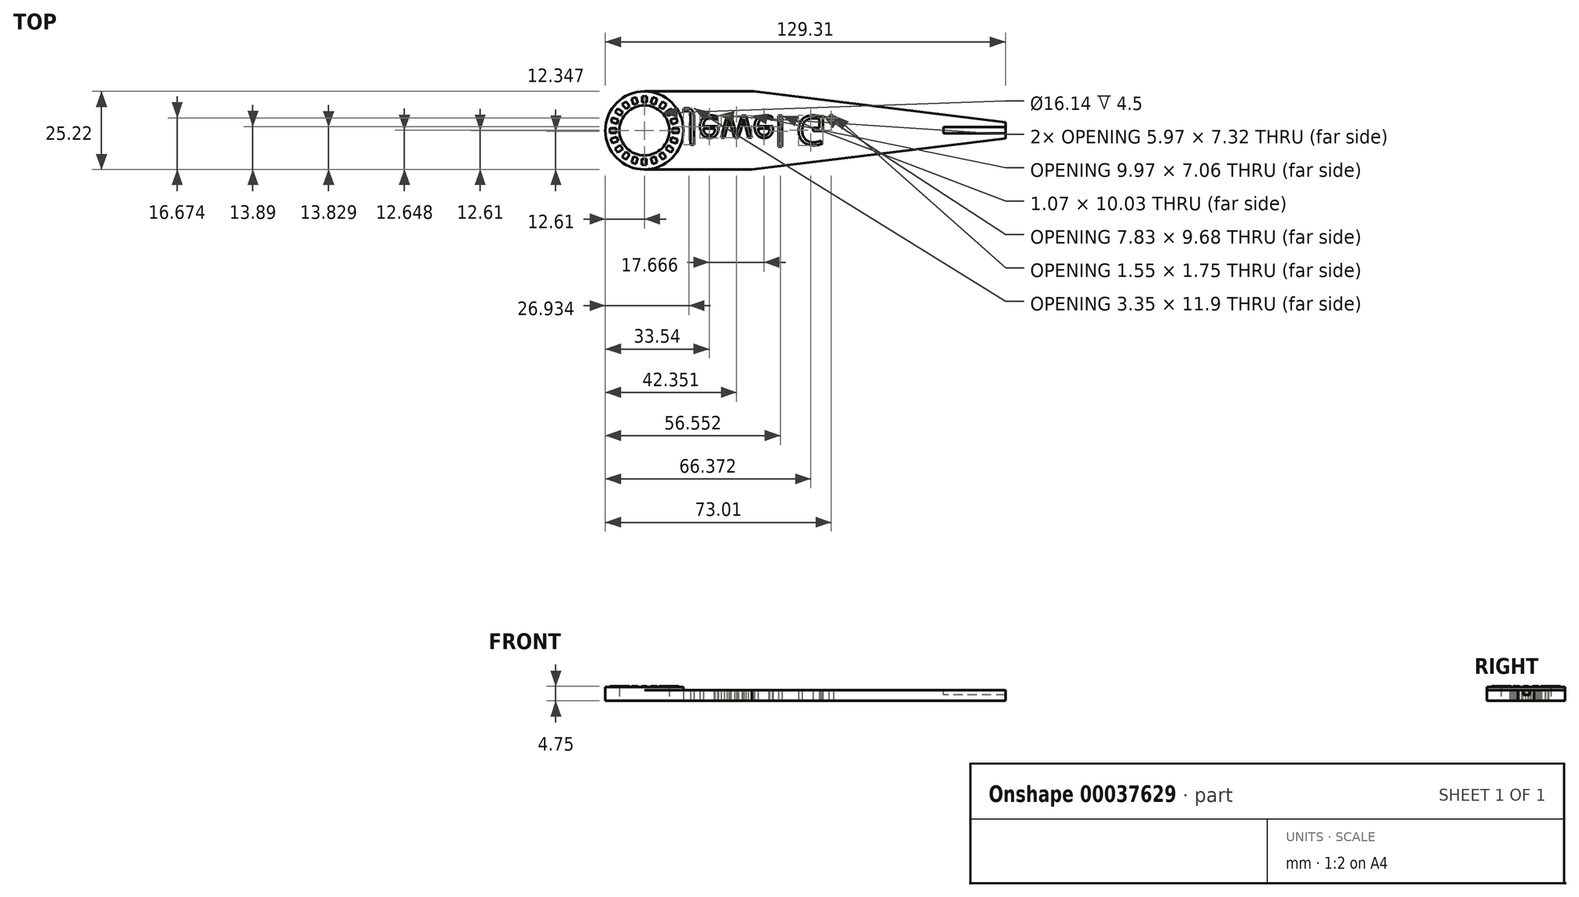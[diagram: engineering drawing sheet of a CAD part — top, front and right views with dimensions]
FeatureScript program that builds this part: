
annotation { "Feature Type Name" : "Feature", "Feature Type Description" : "" }
export const myFeature = defineFeature(function(context is Context, id is Id, definition is map)
    precondition{}
    {
        {
            var Q0;
            Q0=qCreatedBy(makeId("Top.planeOp"),FACE);
            var sketch = newSketch(context, id + "F0", { "sketchPlane" : qUnion([Q0])});
            skCircle(sketch, "E0", {"center": v(0, 0) * mm, "radius": 8.07 * mm});
            skArc(sketch, "E1", {"start": v(0, 12.6) * mm, "mid": v(-12.6, 0) * mm, "end": v(0, -12.6) * mm});
            skLineSegment(sketch, "E2", {"start": v(35.3, 12.6) * mm, "end": v(0, 12.6) * mm});
            skLineSegment(sketch, "E3", {"start": v(34.7, -12.6) * mm, "end": v(0, -12.6) * mm});
            skLineSegment(sketch, "E4", {"start": v(35.3, 12.6) * mm, "end": v(125.73, 12.6) * mm, "construction": true});
            skLineSegment(sketch, "E5", {"start": v(35.3, 12.6) * mm, "end": v(116.7, 2.62) * mm});
            skLineSegment(sketch, "E6.MirrorCS", {"start": v(34.7, -12.6) * mm, "end": v(116.7, -2.62) * mm});
            skLineSegment(sketch, "E7", {"start": v(116.7, 2.62) * mm, "end": v(116.7, -2.62) * mm});
            skSolve(sketch);
        }
        {
            var Q0;
            Q0 = qSketchRegion(id + "F0", true);
            extrude(context, id + "F1", {"entities" : qUnion([Q0]), "depth" : 3.5 * mm});
        }
        {
            var Q0;
            Q0=makeQuery(id+"F1.opExtrude","CAP_FACE",FACE,{"disambiguationData":[OSD([sQuery(id+"F0.wireOp",EDGE,"E0"),sQuery(id+"F0.wireOp",EDGE,"E1"),sQuery(id+"F0.wireOp",EDGE,"E2"),sQuery(id+"F0.wireOp",EDGE,"E3"),sQuery(id+"F0.wireOp",EDGE,"E5"),sQuery(id+"F0.wireOp",EDGE,"E6.MirrorCS"),sQuery(id+"F0.wireOp",EDGE,"E7")])],"isStart":false});
            var sketch = newSketch(context, id + "F2", { "sketchPlane" : qUnion([Q0])});
            skCircle(sketch, "E8", {"center": v(0, 0) * mm, "radius": 8.07 * mm});
            skCircle(sketch, "E9", {"center": v(0, 0) * mm, "radius": 12.6 * mm});
            skSolve(sketch);
        }
        {
            var Q0;
            Q0 = qSketchRegion(id + "F2", true);
            extrude(context, id + "F3", {"entities" : qUnion([Q0]), "operationType" : NewBodyOperationType.ADD, "depth" : 1 * mm});
        }
        {
            var Q0;
            Q0=makeQuery(id+"F3.opExtrude","CAP_FACE",FACE,{"disambiguationData":[OSD([sQuery(id+"F2.wireOp",EDGE,"E8"),sQuery(id+"F2.wireOp",EDGE,"E9")])],"isStart":false});
            var sketch = newSketch(context, id + "F4", { "sketchPlane" : qUnion([Q0])});
            skLineSegment(sketch, "E10.bottom", {"start": v(-0.75, 11.07) * mm, "end": v(0.75, 11.07) * mm});
            skLineSegment(sketch, "E10.top", {"start": v(-0.75, 9.07) * mm, "end": v(0.75, 9.07) * mm});
            skLineSegment(sketch, "E10.left", {"start": v(-0.75, 11.07) * mm, "end": v(-0.75, 9.07) * mm});
            skLineSegment(sketch, "E10.right", {"start": v(0.75, 11.07) * mm, "end": v(0.75, 9.07) * mm});
            skPoint(sketch, "E11", {"position": v(0, 8.07) * mm});
            skLineSegment(sketch, "E12.1.0", {"start": v(-4.14, 10.3) * mm, "end": v(-2.72, 10.77) * mm});
            skLineSegment(sketch, "E12.1.1", {"start": v(-4.14, 10.3) * mm, "end": v(-3.53, 8.4) * mm});
            skLineSegment(sketch, "E12.1.2", {"start": v(-3.53, 8.4) * mm, "end": v(-2.1, 8.87) * mm});
            skLineSegment(sketch, "E12.1.3", {"start": v(-2.72, 10.77) * mm, "end": v(-2.1, 8.87) * mm});
            skLineSegment(sketch, "E12.2.0", {"start": v(-7.14, 8.53) * mm, "end": v(-5.92, 9.4) * mm});
            skLineSegment(sketch, "E12.2.1", {"start": v(-7.14, 8.53) * mm, "end": v(-5.96, 6.9) * mm});
            skLineSegment(sketch, "E12.2.2", {"start": v(-5.96, 6.9) * mm, "end": v(-4.75, 7.8) * mm});
            skLineSegment(sketch, "E12.2.3", {"start": v(-5.92, 9.4) * mm, "end": v(-4.75, 7.8) * mm});
            skLineSegment(sketch, "E12.3.0", {"start": v(-9.43, 5.91) * mm, "end": v(-8.55, 7.13) * mm});
            skLineSegment(sketch, "E12.3.1", {"start": v(-9.43, 5.91) * mm, "end": v(-7.82, 4.74) * mm});
            skLineSegment(sketch, "E12.3.2", {"start": v(-7.82, 4.74) * mm, "end": v(-6.93, 5.95) * mm});
            skLineSegment(sketch, "E12.3.3", {"start": v(-8.55, 7.13) * mm, "end": v(-6.93, 5.95) * mm});
            skLineSegment(sketch, "E12.4.0", {"start": v(-10.8, 2.72) * mm, "end": v(-10.35, 4.14) * mm});
            skLineSegment(sketch, "E12.4.1", {"start": v(-10.8, 2.72) * mm, "end": v(-8.9, 2.1) * mm});
            skLineSegment(sketch, "E12.4.2", {"start": v(-8.9, 2.1) * mm, "end": v(-8.44, 3.52) * mm});
            skLineSegment(sketch, "E12.4.3", {"start": v(-10.35, 4.14) * mm, "end": v(-8.44, 3.52) * mm});
            skLineSegment(sketch, "E12.5.0", {"start": v(-11.13, -0.75) * mm, "end": v(-11.13, 0.75) * mm});
            skLineSegment(sketch, "E12.5.1", {"start": v(-11.13, -0.75) * mm, "end": v(-9.13, -0.75) * mm});
            skLineSegment(sketch, "E12.5.2", {"start": v(-9.13, -0.75) * mm, "end": v(-9.13, 0.75) * mm});
            skLineSegment(sketch, "E12.5.3", {"start": v(-11.13, 0.75) * mm, "end": v(-9.13, 0.75) * mm});
            skLineSegment(sketch, "E12.6.0", {"start": v(-10.36, -4.14) * mm, "end": v(-10.83, -2.72) * mm});
            skLineSegment(sketch, "E12.6.1", {"start": v(-10.36, -4.14) * mm, "end": v(-8.46, -3.53) * mm});
            skLineSegment(sketch, "E12.6.2", {"start": v(-8.46, -3.53) * mm, "end": v(-8.93, -2.1) * mm});
            skLineSegment(sketch, "E12.6.3", {"start": v(-10.83, -2.72) * mm, "end": v(-8.93, -2.1) * mm});
            skLineSegment(sketch, "E12.7.0", {"start": v(-8.59, -7.14) * mm, "end": v(-9.47, -5.92) * mm});
            skLineSegment(sketch, "E12.7.1", {"start": v(-8.59, -7.14) * mm, "end": v(-6.97, -5.96) * mm});
            skLineSegment(sketch, "E12.7.2", {"start": v(-6.97, -5.96) * mm, "end": v(-7.85, -4.75) * mm});
            skLineSegment(sketch, "E12.7.3", {"start": v(-9.47, -5.92) * mm, "end": v(-7.85, -4.75) * mm});
            skLineSegment(sketch, "E12.8.0", {"start": v(-5.97, -9.43) * mm, "end": v(-7.19, -8.55) * mm});
            skLineSegment(sketch, "E12.8.1", {"start": v(-5.97, -9.43) * mm, "end": v(-4.8, -7.82) * mm});
            skLineSegment(sketch, "E12.8.2", {"start": v(-4.8, -7.82) * mm, "end": v(-6.01, -6.93) * mm});
            skLineSegment(sketch, "E12.8.3", {"start": v(-7.19, -8.55) * mm, "end": v(-6.01, -6.93) * mm});
            skLineSegment(sketch, "E12.9.0", {"start": v(-2.78, -10.8) * mm, "end": v(-4.2, -10.35) * mm});
            skLineSegment(sketch, "E12.9.1", {"start": v(-2.78, -10.8) * mm, "end": v(-2.16, -8.9) * mm});
            skLineSegment(sketch, "E12.9.2", {"start": v(-2.16, -8.9) * mm, "end": v(-3.58, -8.44) * mm});
            skLineSegment(sketch, "E12.9.3", {"start": v(-4.2, -10.35) * mm, "end": v(-3.58, -8.44) * mm});
            skLineSegment(sketch, "E12.10.0", {"start": v(0.69, -11.13) * mm, "end": v(-0.81, -11.13) * mm});
            skLineSegment(sketch, "E12.10.1", {"start": v(0.69, -11.13) * mm, "end": v(0.69, -9.13) * mm});
            skLineSegment(sketch, "E12.10.2", {"start": v(0.69, -9.13) * mm, "end": v(-0.81, -9.13) * mm});
            skLineSegment(sketch, "E12.10.3", {"start": v(-0.81, -11.13) * mm, "end": v(-0.81, -9.13) * mm});
            skLineSegment(sketch, "E12.11.0", {"start": v(4.08, -10.36) * mm, "end": v(2.66, -10.83) * mm});
            skLineSegment(sketch, "E12.11.1", {"start": v(4.08, -10.36) * mm, "end": v(3.47, -8.46) * mm});
            skLineSegment(sketch, "E12.11.2", {"start": v(3.47, -8.46) * mm, "end": v(2.04, -8.93) * mm});
            skLineSegment(sketch, "E12.11.3", {"start": v(2.66, -10.83) * mm, "end": v(2.04, -8.93) * mm});
            skLineSegment(sketch, "E12.12.0", {"start": v(7.08, -8.59) * mm, "end": v(5.86, -9.47) * mm});
            skLineSegment(sketch, "E12.12.1", {"start": v(7.08, -8.59) * mm, "end": v(5.9, -6.97) * mm});
            skLineSegment(sketch, "E12.12.2", {"start": v(5.9, -6.97) * mm, "end": v(4.69, -7.85) * mm});
            skLineSegment(sketch, "E12.12.3", {"start": v(5.86, -9.47) * mm, "end": v(4.69, -7.85) * mm});
            skLineSegment(sketch, "E12.13.0", {"start": v(9.37, -5.97) * mm, "end": v(8.5, -7.19) * mm});
            skLineSegment(sketch, "E12.13.1", {"start": v(9.37, -5.97) * mm, "end": v(7.76, -4.8) * mm});
            skLineSegment(sketch, "E12.13.2", {"start": v(7.76, -4.8) * mm, "end": v(6.87, -6.01) * mm});
            skLineSegment(sketch, "E12.13.3", {"start": v(8.5, -7.19) * mm, "end": v(6.87, -6.01) * mm});
            skLineSegment(sketch, "E12.14.0", {"start": v(10.75, -2.78) * mm, "end": v(10.29, -4.2) * mm});
            skLineSegment(sketch, "E12.14.1", {"start": v(10.75, -2.78) * mm, "end": v(8.85, -2.16) * mm});
            skLineSegment(sketch, "E12.14.2", {"start": v(8.85, -2.16) * mm, "end": v(8.38, -3.58) * mm});
            skLineSegment(sketch, "E12.14.3", {"start": v(10.29, -4.2) * mm, "end": v(8.38, -3.58) * mm});
            skLineSegment(sketch, "E12.15.0", {"start": v(11.07, 0.69) * mm, "end": v(11.07, -0.81) * mm});
            skLineSegment(sketch, "E12.15.1", {"start": v(11.07, 0.69) * mm, "end": v(9.07, 0.69) * mm});
            skLineSegment(sketch, "E12.15.2", {"start": v(9.07, 0.69) * mm, "end": v(9.07, -0.81) * mm});
            skLineSegment(sketch, "E12.15.3", {"start": v(11.07, -0.81) * mm, "end": v(9.07, -0.81) * mm});
            skLineSegment(sketch, "E12.16.0", {"start": v(10.3, 4.08) * mm, "end": v(10.77, 2.66) * mm});
            skLineSegment(sketch, "E12.16.1", {"start": v(10.3, 4.08) * mm, "end": v(8.4, 3.47) * mm});
            skLineSegment(sketch, "E12.16.2", {"start": v(8.4, 3.47) * mm, "end": v(8.87, 2.04) * mm});
            skLineSegment(sketch, "E12.16.3", {"start": v(10.77, 2.66) * mm, "end": v(8.87, 2.04) * mm});
            skLineSegment(sketch, "E12.17.0", {"start": v(8.53, 7.08) * mm, "end": v(9.4, 5.86) * mm});
            skLineSegment(sketch, "E12.17.1", {"start": v(8.53, 7.08) * mm, "end": v(6.9, 5.9) * mm});
            skLineSegment(sketch, "E12.17.2", {"start": v(6.9, 5.9) * mm, "end": v(7.8, 4.69) * mm});
            skLineSegment(sketch, "E12.17.3", {"start": v(9.4, 5.86) * mm, "end": v(7.8, 4.69) * mm});
            skLineSegment(sketch, "E12.18.0", {"start": v(5.91, 9.37) * mm, "end": v(7.13, 8.5) * mm});
            skLineSegment(sketch, "E12.18.1", {"start": v(5.91, 9.37) * mm, "end": v(4.74, 7.76) * mm});
            skLineSegment(sketch, "E12.18.2", {"start": v(4.74, 7.76) * mm, "end": v(5.95, 6.87) * mm});
            skLineSegment(sketch, "E12.18.3", {"start": v(7.13, 8.5) * mm, "end": v(5.95, 6.87) * mm});
            skLineSegment(sketch, "E12.19.0", {"start": v(2.72, 10.75) * mm, "end": v(4.14, 10.29) * mm});
            skLineSegment(sketch, "E12.19.1", {"start": v(2.72, 10.75) * mm, "end": v(2.1, 8.85) * mm});
            skLineSegment(sketch, "E12.19.2", {"start": v(2.1, 8.85) * mm, "end": v(3.52, 8.38) * mm});
            skLineSegment(sketch, "E12.19.3", {"start": v(4.14, 10.29) * mm, "end": v(3.52, 8.38) * mm});
            skPoint(sketch, "E12.center", {"position": v(-0.03, -0.03) * mm});
            skSolve(sketch);
        }
        {
            var Q0;
            Q0 = qSketchRegion(id + "F4", true);
            extrude(context, id + "F5", {"entities" : qUnion([Q0]), "operationType" : NewBodyOperationType.ADD, "depth" : .25 * mm});
        }
        {
            var Q0;
            Q0=makeQuery(id+"F1.opExtrude","CAP_FACE",FACE,{"disambiguationData":[OSD([sQuery(id+"F0.wireOp",EDGE,"E0"),sQuery(id+"F0.wireOp",EDGE,"E1"),sQuery(id+"F0.wireOp",EDGE,"E2"),sQuery(id+"F0.wireOp",EDGE,"E3"),sQuery(id+"F0.wireOp",EDGE,"E5"),sQuery(id+"F0.wireOp",EDGE,"E6.MirrorCS"),sQuery(id+"F0.wireOp",EDGE,"E7")])],"isStart":false});
            var sketch = newSketch(context, id + "F6", { "sketchPlane" : qUnion([Q0])});
            skLineSegment(sketch, "E13.bottom", {"start": v(116.7, 1.12) * mm, "end": v(96.7, 1.12) * mm});
            skLineSegment(sketch, "E13.top", {"start": v(116.7, -0.88) * mm, "end": v(96.7, -0.88) * mm});
            skLineSegment(sketch, "E13.left", {"start": v(116.7, 1.12) * mm, "end": v(116.7, -0.88) * mm});
            skLineSegment(sketch, "E13.right", {"start": v(96.7, 1.12) * mm, "end": v(96.7, -0.88) * mm});
            skSolve(sketch);
        }
        {
            var Q0;
            Q0=makeQuery(id+"F6.imprint","IMPRINT",FACE,{"disambiguationData":[TD([[makeQuery(id+"F6.imprint","IMPRINT",EDGE,{"derivedFrom":sQuery(id+"F6.wireOp",EDGE,"E13.bottom")}),1.0]])]});
            extrude(context, id + "F7", {"entities" : qUnion([Q0]), "operationType" : NewBodyOperationType.REMOVE, "oppositeDirection" : true, "depth" : 1.5 * mm});
        }
        {
            var Q0;
            Q0=makeQuery(id+"F1.opExtrude","CAP_EDGE",EDGE,{"disambiguationData":[OSD([sQuery(id+"F0.wireOp",EDGE,"E3")])],"isStart":true});
            cPlane(context, id + "F8", {"entities" : qUnion([Q0]), "cplaneType" : CPlaneType.LINE_ANGLE, "offset" : 150 * mm, "angle" : 270 * degree, "width" : 150 * mm, "height" : 150 * mm});
        }
        {
            var Q0;
            Q0=qCreatedBy(id+"F8.planeOp",FACE);
            var sketch = newSketch(context, id + "F9", { "sketchPlane" : qUnion([Q0])});
            skText(sketch, "E14", { "text": "Jewel G.", "fontName": "OpenSans-Regular.ttf"});
            skLineSegment(sketch, "E15", {"start": v(0, 0) * mm, "end": v(27.36, 0) * mm, "construction": true});
            skPoint(sketch, "E16", {"position": v(13.68, 0) * mm});
            const initialGuessF9  = {"E14": [0.01368, -0.00475, 1, 0, 0.0095]};
            skSetInitialGuess(sketch, initialGuessF9);
            skSolve(sketch);
        }
        {
            var Q0;
            Q0 = qSketchRegion(id + "F9", true);
            extrude(context, id + "F10", {"entities" : qUnion([Q0]), "operationType" : NewBodyOperationType.REMOVE, "endBound" : BoundingType.THROUGH_ALL, "oppositeDirection" : true, "depth" : 25 * mm});
        }
    });
